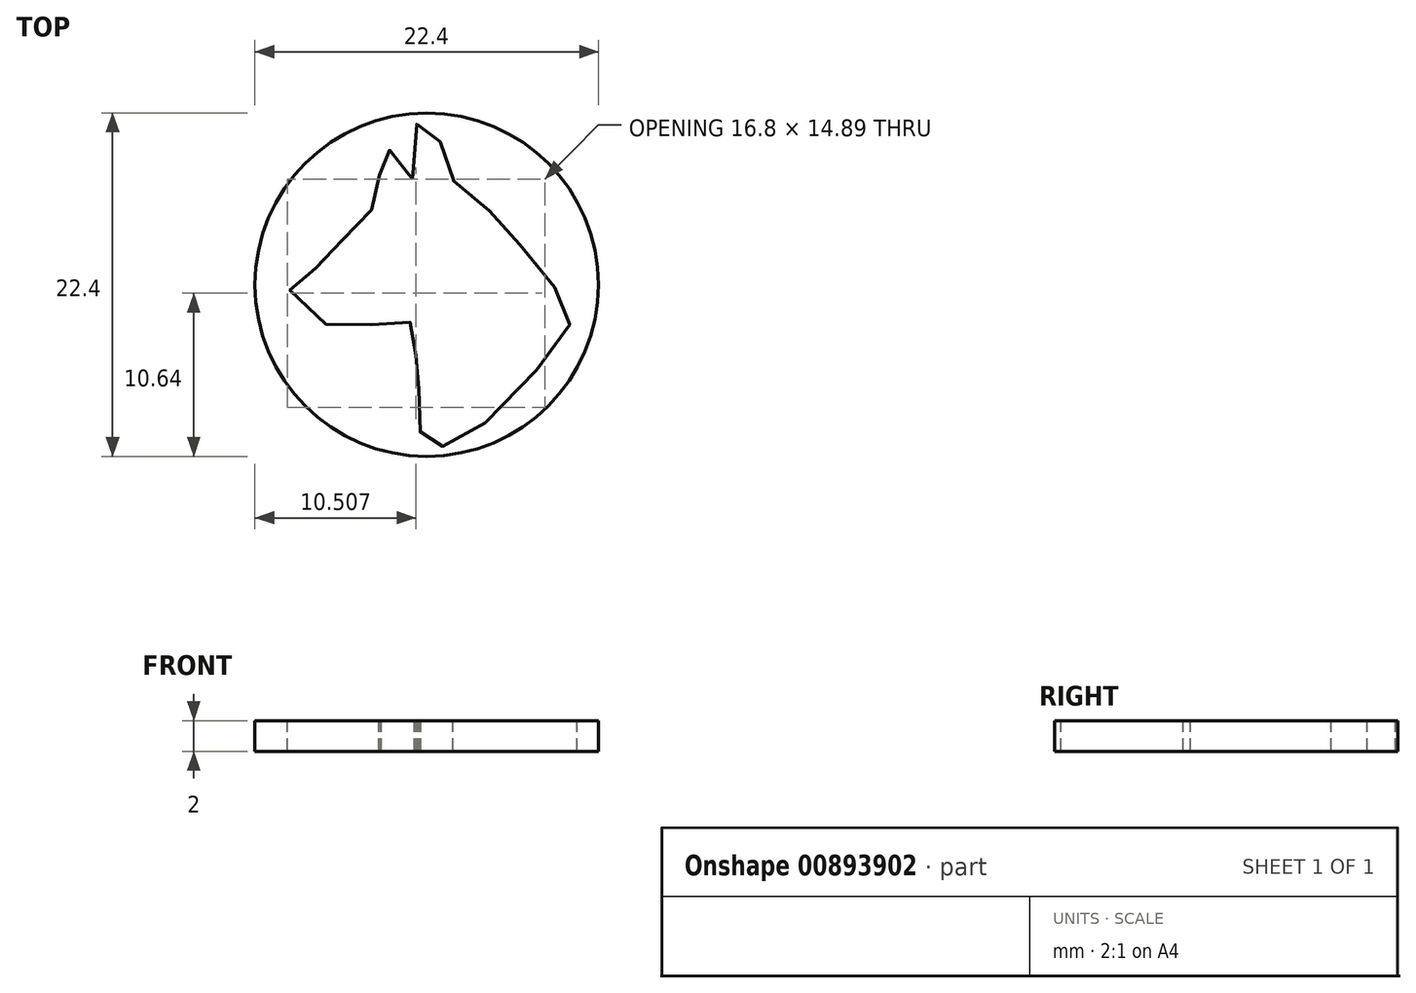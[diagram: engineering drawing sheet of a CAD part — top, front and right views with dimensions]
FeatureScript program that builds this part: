
annotation { "Feature Type Name" : "Feature", "Feature Type Description" : "" }
export const myFeature = defineFeature(function(context is Context, id is Id, definition is map)
    precondition{}
    {
        {
            var Q0;
            Q0=qCreatedBy(makeId("Top.planeOp"),FACE);
            var sketch = newSketch(context, id + "F0", { "sketchPlane" : qUnion([Q0])});
            skCircle(sketch, "E0", {"center": v(0, 0) * mm, "radius": 11.2 * mm});
            skSolve(sketch);
        }
        {
            var Q0;
            Q0=makeQuery(id+"F0.imprint","IMPRINT",FACE,{"disambiguationData":[TD([[makeQuery(id+"F0.imprint","IMPRINT",EDGE,{"derivedFrom":sQuery(id+"F0.wireOp",EDGE,"E0")}),1.0]])]});
            extrude(context, id + "F1", {"entities" : qUnion([Q0]), "depth" : 2 * mm, "offsetDistance" : 25 * mm});
        }
        {
            var Q0;
            Q0=makeQuery(id+"F1.opExtrude","CAP_FACE",FACE,{"disambiguationData":[OSD([sQuery(id+"F0.wireOp",EDGE,"E0")])],"isStart":false});
            var sketch = newSketch(context, id + "F2", { "sketchPlane" : qUnion([Q0])});
            skFitSpline(sketch, "E1", {"points": [v(-0.92, 6.89) * mm, v(-0.77, 8.6) * mm, v(-0.73, 10.07) * mm, v(-0.62, 10.19) * mm, v(-0.63, 10.27) * mm, v(-0.65, 10.97) * mm, v(-0.52, 11) * mm, v(0, 10.46) * mm, v(0.42, 9.94) * mm, v(0.86, 9.34) * mm, v(1.29, 8.45) * mm, v(1.54, 7.8) * mm, v(1.67, 7.2) * mm, v(1.7, 6.78) * mm, v(1.82, 6.73) * mm, v(2.3, 6.46) * mm, v(2.7, 6.17) * mm, v(3.46, 5.5) * mm, v(4.16, 4.77) * mm, v(4.74, 4.17) * mm, v(5.14, 3.75) * mm, v(5.62, 3.22) * mm, v(6.02, 2.67) * mm, v(6.45, 2.24) * mm, v(7.11, 1.38) * mm, v(7.91, 0.38) * mm, v(8.68, -0.63) * mm, v(9.22, -1.25) * mm, v(9.76, -1.86) * mm, v(9.6, -2.2) * mm, v(9.06, -3.04) * mm, v(8.5, -3.82) * mm, v(7.8, -4.73) * mm, v(7.04, -5.7) * mm, v(5.44, -7.5) * mm, v(4.3, -8.6) * mm, v(3.2, -9.48) * mm, v(2.46, -10) * mm, v(1.88, -10.27) * mm, v(1.21, -10.48) * mm, v(0.8, -10.64) * mm, v(0.26, -10.73) * mm, v(-0.4, -10.78) * mm, v(-0.42, -10.43) * mm, v(-0.42, -9.65) * mm, v(-0.4, -8.86) * mm, v(-0.45, -7.98) * mm, v(-0.48, -7.53) * mm, v(-0.53, -7.02) * mm, v(-0.51, -6.64) * mm, v(-0.52, -6.25) * mm, v(-0.59, -5.94) * mm, v(-0.63, -5.42) * mm, v(-0.64, -4.78) * mm, v(-0.7, -4.68) * mm, v(-0.71, -4.06) * mm, v(-0.73, -3.57) * mm, v(-0.82, -3.36) * mm, v(-0.79, -2.65) * mm, v(-0.79, -2.55) * mm, v(-1.26, -2.42) * mm, v(-1.67, -2.37) * mm, v(-2.17, -2.37) * mm, v(-2.8, -2.47) * mm, v(-3.29, -2.55) * mm, v(-3.88, -2.67) * mm, v(-4.51, -2.8) * mm, v(-5.24, -2.83) * mm, v(-6.01, -2.76) * mm, v(-6.87, -2.42) * mm, v(-7.61, -1.82) * mm, v(-8.15, -1.32) * mm, v(-8.75, -0.6) * mm, v(-9.09, -0.15) * mm, v(-9.11, 0) * mm, v(-8.81, 0.23) * mm, v(-8.25, 0.58) * mm, v(-7.56, 0.93) * mm, v(-6.9, 1.25) * mm, v(-6.51, 1.5) * mm, v(-6.04, 1.92) * mm, v(-5.77, 2.3) * mm, v(-5.53, 2.86) * mm, v(-5.19, 3.37) * mm, v(-4.78, 3.85) * mm, v(-4.36, 4.28) * mm, v(-3.9, 4.66) * mm, v(-3.46, 5) * mm, v(-3.3, 5.18) * mm, v(-3, 5.3) * mm, v(-3.02, 5.4) * mm, v(-3.04, 5.88) * mm, v(-3.08, 7.15) * mm, v(-3.12, 8.29) * mm, v(-3.13, 9.07) * mm, v(-3.06, 9.16) * mm, v(-2.81, 8.99) * mm, v(-2.38, 8.75) * mm, v(-1.95, 8.36) * mm, v(-1.44, 7.81) * mm, v(-1.07, 7.17) * mm, v(-1.01, 6.83) * mm, v(-0.92, 6.89) * mm]});
            skSolve(sketch);
        }
        {
            var Q0;
            Q0 = qSketchRegion(id + "F2", true);
            extrude(context, id + "F3", {"entities" : qUnion([Q0]), "operationType" : NewBodyOperationType.REMOVE, "oppositeDirection" : true, "depth" : 25 * mm, "offsetDistance" : 25 * mm});
        }
    });
